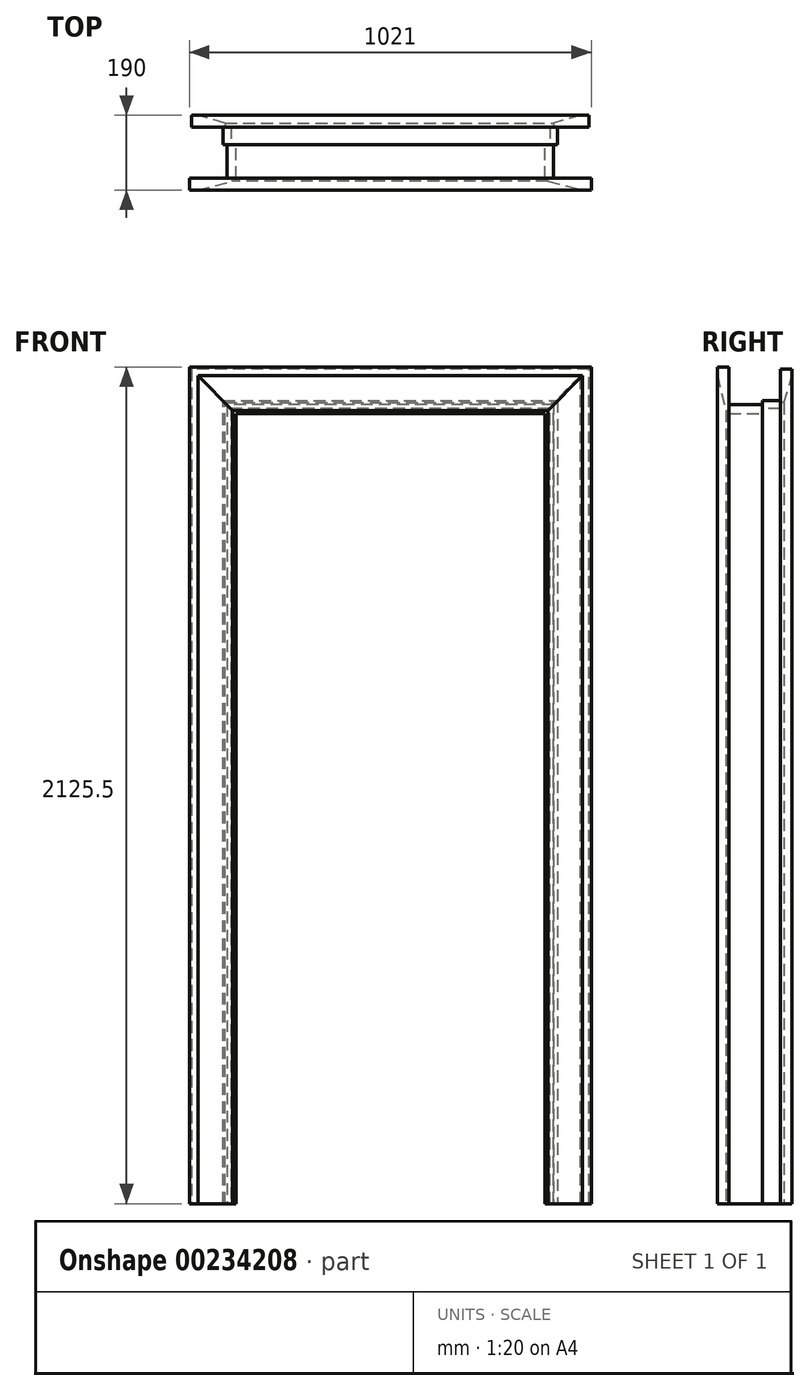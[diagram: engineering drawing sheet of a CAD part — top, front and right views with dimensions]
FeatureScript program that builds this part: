
annotation { "Feature Type Name" : "Feature", "Feature Type Description" : "" }
export const myFeature = defineFeature(function(context is Context, id is Id, definition is map)
    precondition{}
    {
        {
            var Q0;
            Q0=qCreatedBy(makeId("Front.planeOp"),FACE);
            var sketch = newSketch(context, id + "F0", { "sketchPlane" : qUnion([Q0])});
            skLineSegment(sketch, "E0", {"start": v(0, 0) * mm, "end": v(0, 2007.5) * mm});
            skLineSegment(sketch, "E1", {"start": v(0, 2007.5) * mm, "end": v(785, 2007.5) * mm});
            skLineSegment(sketch, "E2", {"start": v(785, 2007.5) * mm, "end": v(785, 0) * mm});
            skLineSegment(sketch, "E3", {"start": v(785, 0) * mm, "end": v(807.5, 0) * mm});
            skLineSegment(sketch, "E4", {"start": v(807.5, 0) * mm, "end": v(807.5, 2030) * mm});
            skLineSegment(sketch, "E5", {"start": v(807.5, 2030) * mm, "end": v(-22.5, 2030) * mm});
            skLineSegment(sketch, "E6", {"start": v(-22.5, 2030) * mm, "end": v(-22.5, 0) * mm});
            skLineSegment(sketch, "E7", {"start": v(-22.5, 0) * mm, "end": v(0, 0) * mm});
            skSolve(sketch);
        }
        {
            var Q0;
            Q0=makeQuery(id+"F0.imprint","IMPRINT",FACE,{"disambiguationData":[TD([[makeQuery(id+"F0.imprint","IMPRINT",EDGE,{"derivedFrom":sQuery(id+"F0.wireOp",EDGE,"E0")}),1.0]])]});
            extrude(context, id + "F1", {"entities" : qUnion([Q0]), "depth" : 85 * mm});
        }
        {
            var Q0;
            Q0=makeQuery(id+"F1.opExtrude","CAP_FACE",FACE,{"disambiguationData":[OSD([sQuery(id+"F0.wireOp",EDGE,"E0"),sQuery(id+"F0.wireOp",EDGE,"E1"),sQuery(id+"F0.wireOp",EDGE,"E2"),sQuery(id+"F0.wireOp",EDGE,"E3"),sQuery(id+"F0.wireOp",EDGE,"E4"),sQuery(id+"F0.wireOp",EDGE,"E5"),sQuery(id+"F0.wireOp",EDGE,"E6"),sQuery(id+"F0.wireOp",EDGE,"E7")])],"isStart":true});
            var sketch = newSketch(context, id + "F2", { "sketchPlane" : qUnion([Q0])});
            skLineSegment(sketch, "E8", {"start": v(22.5, 0) * mm, "end": v(32.5, 0) * mm});
            skLineSegment(sketch, "E9", {"start": v(32.5, 0) * mm, "end": v(32.5, 2040) * mm});
            skLineSegment(sketch, "E10", {"start": v(32.5, 2040) * mm, "end": v(-817.5, 2040) * mm});
            skLineSegment(sketch, "E11", {"start": v(-817.5, 2040) * mm, "end": v(-817.5, 0) * mm});
            skLineSegment(sketch, "E12", {"start": v(-817.5, 0) * mm, "end": v(-807.5, 0) * mm});
            skLineSegment(sketch, "E13", {"start": v(-807.5, 0) * mm, "end": v(-807.5, 2030) * mm, "construction": true});
            skLineSegment(sketch, "E14", {"start": v(-807.5, 2030) * mm, "end": v(22.5, 2030) * mm, "construction": true});
            skLineSegment(sketch, "E15", {"start": v(22.5, 2030) * mm, "end": v(22.5, 0) * mm, "construction": true});
            skLineSegment(sketch, "E16", {"start": v(-807.5, 0) * mm, "end": v(-797.5, 0) * mm});
            skLineSegment(sketch, "E17", {"start": v(-797.5, 0) * mm, "end": v(-797.5, 2020) * mm});
            skLineSegment(sketch, "E18", {"start": v(-797.5, 2020) * mm, "end": v(12.5, 2020) * mm});
            skLineSegment(sketch, "E19", {"start": v(12.5, 2020) * mm, "end": v(12.5, 0) * mm});
            skLineSegment(sketch, "E20", {"start": v(12.5, 0) * mm, "end": v(22.5, 0) * mm});
            skSolve(sketch);
        }
        {
            var Q0;
            Q0 = qSketchRegion(id + "F2", true);
            extrude(context, id + "F3", {"entities" : qUnion([Q0]), "operationType" : NewBodyOperationType.ADD, "depth" : 45 * mm});
        }
        {
            var Q0;
            Q0=makeQuery(id+"F3.opExtrude","CAP_FACE",FACE,{"disambiguationData":[OSD([sQuery(id+"F2.wireOp",EDGE,"E8"),sQuery(id+"F2.wireOp",EDGE,"E9"),sQuery(id+"F2.wireOp",EDGE,"E10"),sQuery(id+"F2.wireOp",EDGE,"E11"),sQuery(id+"F2.wireOp",EDGE,"E12"),sQuery(id+"F2.wireOp",EDGE,"E13"),sQuery(id+"F2.wireOp",EDGE,"E14"),sQuery(id+"F2.wireOp",EDGE,"E15")])],"isStart":false});
            var sketch = newSketch(context, id + "F4", { "sketchPlane" : qUnion([Q0])});
            skLineSegment(sketch, "E21", {"start": v(32.5, 2040) * mm, "end": v(-817.5, 2040) * mm, "construction": true});
            skLineSegment(sketch, "E22", {"start": v(-817.5, 2040) * mm, "end": v(-817.5, 0) * mm, "construction": true});
            skLineSegment(sketch, "E23", {"start": v(-817.5, 0) * mm, "end": v(-897.5, 0) * mm});
            skLineSegment(sketch, "E24", {"start": v(-897.5, 0) * mm, "end": v(-897.5, 2120) * mm});
            skLineSegment(sketch, "E25", {"start": v(-897.5, 2120) * mm, "end": v(112.5, 2120) * mm});
            skLineSegment(sketch, "E26", {"start": v(112.5, 2120) * mm, "end": v(112.5, 0) * mm});
            skLineSegment(sketch, "E27", {"start": v(112.5, 0) * mm, "end": v(32.5, 0) * mm});
            skLineSegment(sketch, "E28", {"start": v(32.5, 0) * mm, "end": v(32.5, 2040) * mm, "construction": true});
            skLineSegment(sketch, "E29", {"start": v(32.5, 0) * mm, "end": v(27.5, 0) * mm});
            skLineSegment(sketch, "E30", {"start": v(27.5, 0) * mm, "end": v(27.5, 2035) * mm});
            skLineSegment(sketch, "E31", {"start": v(27.5, 2035) * mm, "end": v(-807.5, 2035) * mm});
            skLineSegment(sketch, "E32", {"start": v(-807.5, 2035) * mm, "end": v(-807.5, 0) * mm});
            skPoint(sketch, "E32.endSnap0", {"position": v(-807.5, 0) * mm});
            skLineSegment(sketch, "E33", {"start": v(-807.5, 0) * mm, "end": v(-817.5, 0) * mm});
            skSolve(sketch);
        }
        {
            var Q0;
            Q0 = qSketchRegion(id + "F4", true);
            extrude(context, id + "F5", {"entities" : qUnion([Q0]), "operationType" : NewBodyOperationType.ADD, "depth" : 30 * mm});
        }
        {
            var Q0;
            Q0=makeQuery(id+"F5.opExtrude","CAP_EDGE",EDGE,{"disambiguationData":[OSD([sQuery(id+"F4.wireOp",EDGE,"E31")])],"isStart":false});
            var Q1;
            Q1=makeQuery(id+"F5.opExtrude","CAP_EDGE",EDGE,{"disambiguationData":[OSD([sQuery(id+"F4.wireOp",EDGE,"E30")])],"isStart":false});
            var Q2;
            Q2=makeQuery(id+"F5.opExtrude","CAP_EDGE",EDGE,{"disambiguationData":[OSD([sQuery(id+"F4.wireOp",EDGE,"E32")])],"isStart":false});
            chamfer(context, id + "F6", {"entities" : qUnion([Q0, Q1, Q2]), "chamferType" : ChamferType.TWO_OFFSETS, "width1" : 20 * mm, "oppositeDirection" : false, "width2" : 68 * mm, "tangentPropagation" : true});
        }
        {
            var Q0;
            Q0=makeQuery(id+"F1.opExtrude","CAP_FACE",FACE,{"disambiguationData":[OSD([sQuery(id+"F0.wireOp",EDGE,"E0"),sQuery(id+"F0.wireOp",EDGE,"E1"),sQuery(id+"F0.wireOp",EDGE,"E2"),sQuery(id+"F0.wireOp",EDGE,"E3"),sQuery(id+"F0.wireOp",EDGE,"E4"),sQuery(id+"F0.wireOp",EDGE,"E5"),sQuery(id+"F0.wireOp",EDGE,"E6"),sQuery(id+"F0.wireOp",EDGE,"E7")])],"isStart":false});
            var sketch = newSketch(context, id + "F7", { "sketchPlane" : qUnion([Q0])});
            skLineSegment(sketch, "E34", {"start": v(-8, 0) * mm, "end": v(-118, 0) * mm});
            skPoint(sketch, "E34.endSnap0", {"position": v(-11.25, 0) * mm});
            skLineSegment(sketch, "E35", {"start": v(-118, 0) * mm, "end": v(-118, 2125.5) * mm});
            skLineSegment(sketch, "E36", {"start": v(-118, 2125.5) * mm, "end": v(903, 2125.5) * mm});
            skLineSegment(sketch, "E37", {"start": v(903, 2125.5) * mm, "end": v(903, 0) * mm});
            skLineSegment(sketch, "E38", {"start": v(903, 0) * mm, "end": v(793, 0) * mm});
            skLineSegment(sketch, "E39", {"start": v(793, 0) * mm, "end": v(793, 2015.5) * mm});
            skLineSegment(sketch, "E40", {"start": v(793, 2015.5) * mm, "end": v(-8, 2015.5) * mm});
            skLineSegment(sketch, "E41", {"start": v(-8, 2015.5) * mm, "end": v(-8, 0) * mm});
            skSolve(sketch);
        }
        {
            var Q0;
            Q0 = qSketchRegion(id + "F7", true);
            extrude(context, id + "F8", {"entities" : qUnion([Q0]), "operationType" : NewBodyOperationType.ADD, "depth" : 30 * mm});
        }
        {
            var Q0;
            Q0=makeQuery(id+"F8.opExtrude","CAP_EDGE",EDGE,{"disambiguationData":[OSD([sQuery(id+"F7.wireOp",EDGE,"E39")])],"isStart":false});
            var Q1;
            Q1=makeQuery(id+"F8.opExtrude","CAP_EDGE",EDGE,{"disambiguationData":[OSD([sQuery(id+"F7.wireOp",EDGE,"E40")])],"isStart":false});
            var Q2;
            Q2=makeQuery(id+"F8.opExtrude","CAP_EDGE",EDGE,{"disambiguationData":[OSD([sQuery(id+"F7.wireOp",EDGE,"E41")])],"isStart":false});
            chamfer(context, id + "F9", {"entities" : qUnion([Q0, Q1, Q2]), "chamferType" : ChamferType.TWO_OFFSETS, "width1" : 22 * mm, "oppositeDirection" : false, "width2" : 88 * mm, "tangentPropagation" : true});
        }
    });
